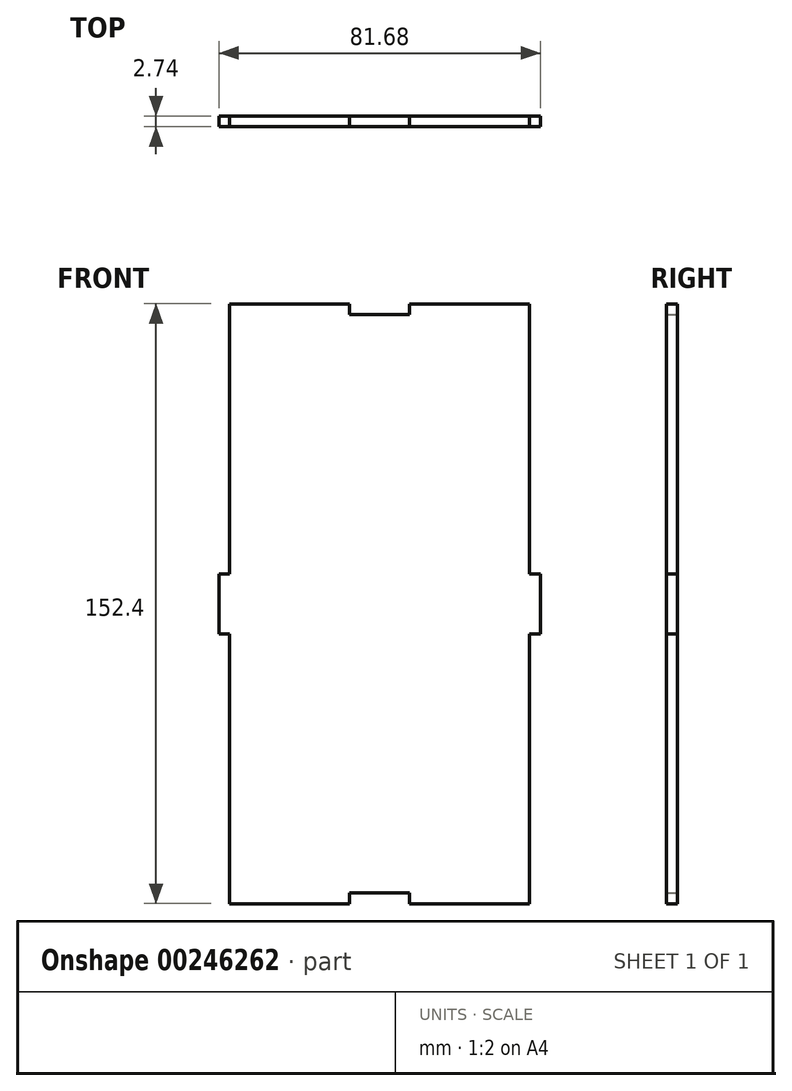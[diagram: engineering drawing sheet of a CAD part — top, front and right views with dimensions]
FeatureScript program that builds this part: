
annotation { "Feature Type Name" : "Feature", "Feature Type Description" : "" }
export const myFeature = defineFeature(function(context is Context, id is Id, definition is map)
    precondition{}
    {
        {
            var Q0;
            Q0=qCreatedBy(makeId("Front.planeOp"),FACE);
            var sketch = newSketch(context, id + "F0", { "sketchPlane" : qUnion([Q0])});
            skLineSegment(sketch, "E0.bottom", {"start": v(-38.1, 84.25) * mm, "end": v(38.1, 84.25) * mm});
            skLineSegment(sketch, "E0.top", {"start": v(-38.1, -68.15) * mm, "end": v(38.1, -68.15) * mm});
            skLineSegment(sketch, "E0.left", {"start": v(-38.1, 84.25) * mm, "end": v(-38.1, -68.15) * mm});
            skLineSegment(sketch, "E0.right", {"start": v(38.1, 84.25) * mm, "end": v(38.1, -68.15) * mm});
            skLineSegment(sketch, "E1", {"start": v(-40.84, 15.67) * mm, "end": v(-38.1, 15.67) * mm});
            skLineSegment(sketch, "E2.MirrorCS", {"start": v(-40.84, 0.43) * mm, "end": v(-38.1, 0.43) * mm});
            skLineSegment(sketch, "E3", {"start": v(-40.84, 15.67) * mm, "end": v(-40.84, 0.43) * mm});
            skLineSegment(sketch, "E4", {"start": v(0, 84.25) * mm, "end": v(0, -68.15) * mm, "construction": true});
            skLineSegment(sketch, "E5.MirrorCS", {"start": v(40.84, 15.67) * mm, "end": v(38.1, 15.67) * mm});
            skLineSegment(sketch, "E6.MirrorCS", {"start": v(40.84, 15.67) * mm, "end": v(40.84, 0.43) * mm});
            skLineSegment(sketch, "E7.MirrorCS", {"start": v(40.84, 0.43) * mm, "end": v(38.1, 0.43) * mm});
            skLineSegment(sketch, "E8", {"start": v(-38.1, 8.05) * mm, "end": v(38.1, 8.05) * mm, "construction": true});
            skLineSegment(sketch, "E9", {"start": v(-7.62, 81.5) * mm, "end": v(-7.62, 84.25) * mm});
            skLineSegment(sketch, "E10.MirrorCS", {"start": v(7.62, 81.5) * mm, "end": v(7.62, 84.25) * mm});
            skLineSegment(sketch, "E11", {"start": v(-7.62, 81.5) * mm, "end": v(7.62, 81.5) * mm});
            skLineSegment(sketch, "E12.MirrorCS", {"start": v(-7.62, -65.41) * mm, "end": v(7.62, -65.41) * mm});
            skLineSegment(sketch, "E13.MirrorCS", {"start": v(7.62, -65.41) * mm, "end": v(7.62, -68.15) * mm});
            skLineSegment(sketch, "E14.MirrorCS", {"start": v(-7.62, -65.41) * mm, "end": v(-7.62, -68.15) * mm});
            skSolve(sketch);
        }
        {
            var Q0;
            {var subQ9=sQuery(id+"F0.wireOp",EDGE,"E0.right");Q0=makeQuery(id+"F0.imprint","IMPRINT",FACE,{"disambiguationData":[TD([[makeQuery(id+"F0.imprint","IMPRINT",EDGE,{"derivedFrom":subQ9}),-1.0]])]});}
            var Q1;
            {var subQ0=sQuery(id+"F0.wireOp",EDGE,"E1");Q1=makeQuery(id+"F0.imprint","IMPRINT",FACE,{"disambiguationData":[TD([[makeQuery(id+"F0.imprint","IMPRINT",EDGE,{"derivedFrom":subQ0}),-1.0]])]});}
            var Q2;
            {var subQ0=sQuery(id+"F0.wireOp",EDGE,"E5.MirrorCS");Q2=makeQuery(id+"F0.imprint","IMPRINT",FACE,{"disambiguationData":[TD([[makeQuery(id+"F0.imprint","IMPRINT",EDGE,{"derivedFrom":subQ0}),1.0]])]});}
            extrude(context, id + "F1", {"entities" : qUnion([Q0, Q1, Q2]), "depth" : 2.74 * mm});
        }
    });
